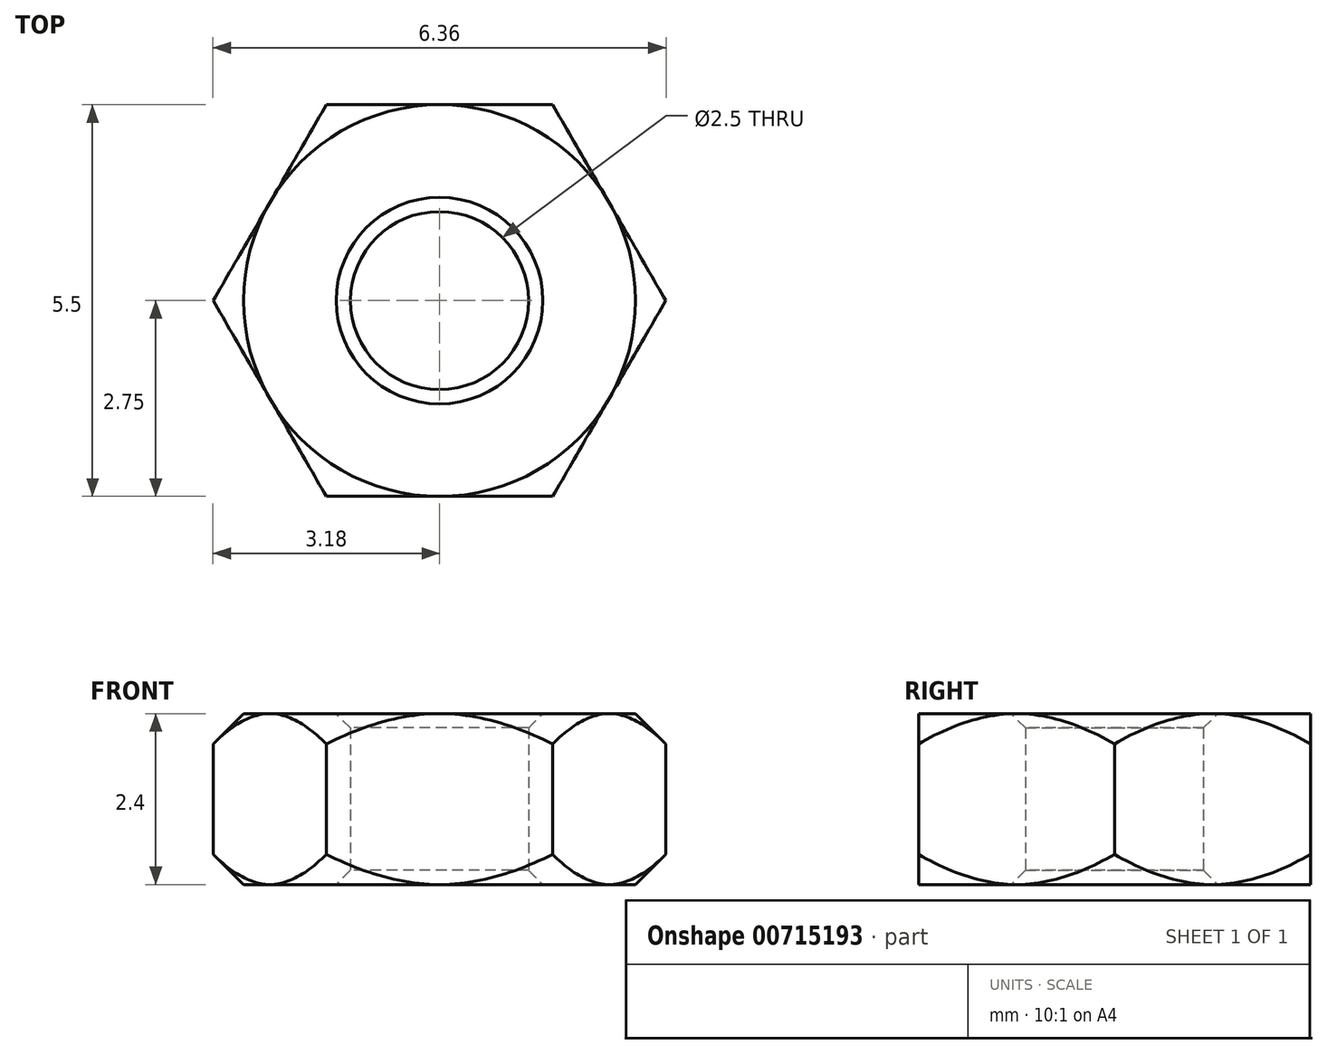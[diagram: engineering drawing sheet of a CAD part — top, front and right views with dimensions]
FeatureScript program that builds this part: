
annotation { "Feature Type Name" : "Feature", "Feature Type Description" : "" }
export const myFeature = defineFeature(function(context is Context, id is Id, definition is map)
    precondition{}
    {
        {
            var Q0;
            Q0=qCreatedBy(makeId("Top.planeOp"),FACE);
            var sketch = newSketch(context, id + "F0", { "sketchPlane" : qUnion([Q0])});
            skCircle(sketch, "E0.cCircle", {"center": v(0, 0) * mm, "radius": 2.75 * mm, "construction": true});
            skLineSegment(sketch, "E0.0", {"start": v(-1.59, 2.75) * mm, "end": v(1.59, 2.75) * mm});
            skLineSegment(sketch, "E0.1", {"start": v(1.59, 2.75) * mm, "end": v(3.18, 0) * mm});
            skLineSegment(sketch, "E0.2", {"start": v(3.18, 0) * mm, "end": v(1.59, -2.75) * mm});
            skLineSegment(sketch, "E0.3", {"start": v(1.59, -2.75) * mm, "end": v(-1.59, -2.75) * mm});
            skLineSegment(sketch, "E0.4", {"start": v(-1.59, -2.75) * mm, "end": v(-3.18, 0) * mm});
            skLineSegment(sketch, "E0.5", {"start": v(-3.18, 0) * mm, "end": v(-1.59, 2.75) * mm});
            skPoint(sketch, "E0.0.midPoint", {"position": v(0, 2.75) * mm});
            skCircle(sketch, "E1", {"center": v(0, 0) * mm, "radius": 1.25 * mm});
            skSolve(sketch);
        }
        {
            var Q0;
            Q0=makeQuery(id+"F0.imprint","IMPRINT",FACE,{"disambiguationData":[TD([[makeQuery(id+"F0.imprint","IMPRINT",EDGE,{"derivedFrom":sQuery(id+"F0.wireOp",EDGE,"E0.0")}),-1.0]])]});
            extrude(context, id + "F1", {"entities" : qUnion([Q0]), "depth" : 2.4 * mm, "offsetDistance" : 25 * mm});
        }
        {
            var Q0;
            Q0=makeQuery(id+"F1.opExtrude","CAP_EDGE",EDGE,{"disambiguationData":[OSD([sQuery(id+"F0.wireOp",EDGE,"E1")])],"isStart":false});
            var Q1;
            Q1=makeQuery(id+"F1.opExtrude","CAP_EDGE",EDGE,{"disambiguationData":[OSD([sQuery(id+"F0.wireOp",EDGE,"E1")])],"isStart":true});
            chamfer(context, id + "F2", {"entities" : qUnion([Q0, Q1]), "width" : 0.2 * mm, "tangentPropagation" : true});
        }
        {
            var Q0;
            Q0=qCreatedBy(makeId("Front.planeOp"),FACE);
            var sketch = newSketch(context, id + "F3", { "sketchPlane" : qUnion([Q0])});
            skLineSegment(sketch, "E2", {"start": v(0, 0) * mm, "end": v(0, 3.7) * mm, "construction": true});
            skLineSegment(sketch, "E3", {"start": v(2.75, 0) * mm, "end": v(3.38, 0.63) * mm});
            skLineSegment(sketch, "E4", {"start": v(3.38, 0.63) * mm, "end": v(3.38, 1.77) * mm});
            skLineSegment(sketch, "E5", {"start": v(3.38, 1.77) * mm, "end": v(2.75, 2.4) * mm});
            skLineSegment(sketch, "E6", {"start": v(2.75, 2.4) * mm, "end": v(2.75, 2.74) * mm});
            skLineSegment(sketch, "E7", {"start": v(2.75, 2.74) * mm, "end": v(3.74, 2.74) * mm});
            skLineSegment(sketch, "E8", {"start": v(3.74, 2.74) * mm, "end": v(3.74, 0) * mm});
            skLineSegment(sketch, "E9", {"start": v(3.74, 0) * mm, "end": v(2.75, 0) * mm});
            skSolve(sketch);
        }
        {
            var Q0;
            Q0=makeQuery(id+"F3.imprint","IMPRINT",FACE,{"disambiguationData":[TD([[makeQuery(id+"F3.imprint","IMPRINT",EDGE,{"derivedFrom":sQuery(id+"F3.wireOp",EDGE,"E3")}),-1.0]])]});
            var Q1;
            Q1=sQuery(id+"F3.wireOp",EDGE,"E2");
            revolve(context, id + "F4", {"operationType" : NewBodyOperationType.REMOVE, "surfaceOperationType" : NewSurfaceOperationType.NEW, "entities" : qUnion([Q0]), "axis" : qUnion([Q1]), "revolveType" : RevolveType.FULL, "oppositeDirection" : true});
        }
    });
